# Revit family: UCB
name_source: partatom
category: Lighting Fixtures
units: mm (PartAtom-declared; Revit-internal decimal feet)

## family parameters
Cut with Voids When Loaded = No
Host = Face
Light Source = No
OmniClass Number = 23.80.70.14
OmniClass Title = Luminaries for External Lighting
Part Type = Normal
Room Calculation Point = No
Round Connector Dimension = Use Diameter
Shared = No

## types (13) — shared parameters
Apparent Load = 32 VA
Default Elevation = 48 "
Description = The Universe Collection® is a complete family of customizable decorative luminaries that transcend architectural styles past and present.
Lamp = LED
Light Bulb Material = Glass-Frosted
Load Classification = Lighting
Manufacturer = Architectural Area Lighting
Model = UCB – Universe Bollard
URL = https://www.currentlighting.com
Wattage Comments = 32W

## per-type parameters (varying)
| type | Finish |
| UCB- ATG | Aluminum-Antique Green |
| UCB- AWT | Aluminum-Artic White |
| UCB- BLK | Aluminum-Black |
| UCB- MTB | Aluminum-Matte Black |
| UCB- DGN | Aluminum-Dark Green |
| UCB- DBZ | Aluminum-Dark Bronze |
| UCB- WRZ | Aluminum-Weathered Bronze |
| UCB- BRM | Aluminum-Metalic Bronze |
| UCB- VBL | Aluminum-Verde Blue |
| UCB- CRT | Aluminum-Corten |
| UCB- MAL | Aluminum-Matte |
| UCB- MDG | Aluminum-Medium Grey |
| UCB- LGY | Aluminum-Light Grey |

## geometry (parser evidence)
native form markers: Blend x58, Sweep x10
no freeform markers — native parametric forms only
